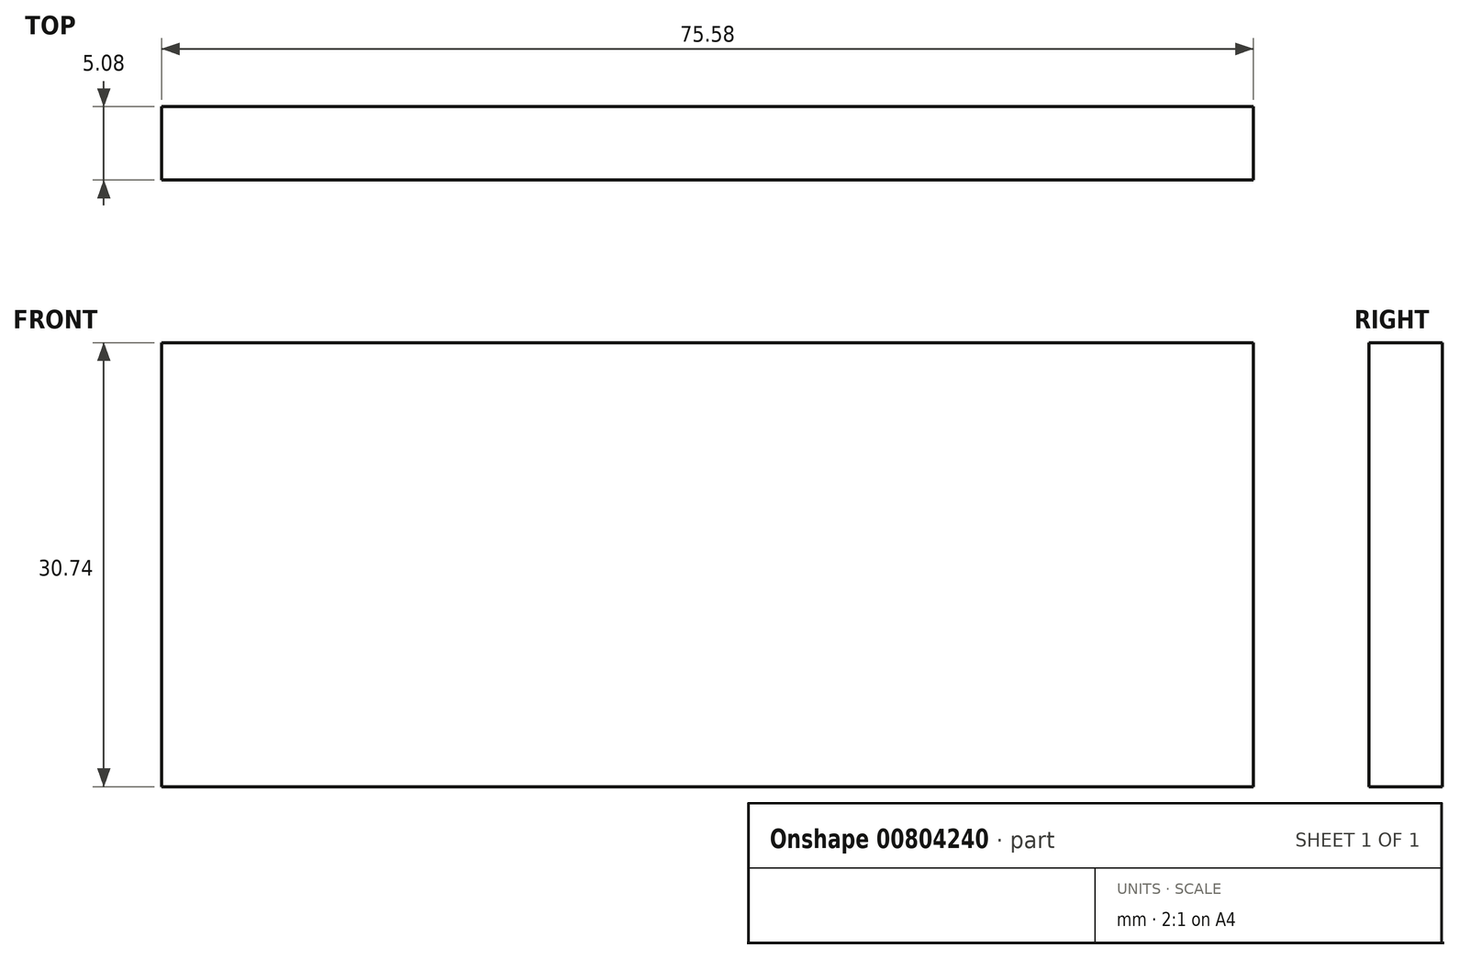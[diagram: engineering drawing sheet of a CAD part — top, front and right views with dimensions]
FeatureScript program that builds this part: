
annotation { "Feature Type Name" : "Feature", "Feature Type Description" : "" }
export const myFeature = defineFeature(function(context is Context, id is Id, definition is map)
    precondition{}
    {
        {
            var Q0;
            Q0=qCreatedBy(makeId("Front.planeOp"),FACE);
            var sketch = newSketch(context, id + "F0", { "sketchPlane" : qUnion([Q0])});
            skLineSegment(sketch, "E0.top", {"start": v(0, 30.74) * mm, "end": v(75.58, 30.74) * mm});
            skLineSegment(sketch, "E0.right", {"start": v(75.58, 0) * mm, "end": v(75.58, 30.74) * mm});
            skLineSegment(sketch, "E1", {"start": v(0, 30.74) * mm, "end": v(0, 0) * mm});
            skLineSegment(sketch, "E2", {"start": v(75.58, 0) * mm, "end": v(0, 0) * mm});
            skSolve(sketch);
        }
        {
            var Q0;
            Q0=makeQuery(id+"F0.imprint","IMPRINT",FACE,{"disambiguationData":[TD([[makeQuery(id+"F0.imprint","IMPRINT",EDGE,{"derivedFrom":sQuery(id+"F0.wireOp",EDGE,"E0.top")}),-1.0]])]});
            extrude(context, id + "F1", {"entities" : qUnion([Q0]), "depth" : 5.08 * mm, "offsetDistance" : 25.4 * mm});
        }
        {
            var Q0;
            Q0=qCreatedBy(makeId("Front.planeOp"),FACE);
            var sketch = newSketch(context, id + "F2", { "sketchPlane" : qUnion([Q0])});
            skLineSegment(sketch, "E3.bottom", {"start": v(6.42, 26.88) * mm, "end": v(69.57, 26.88) * mm});
            skLineSegment(sketch, "E3.top", {"start": v(6.42, 3.87) * mm, "end": v(69.57, 3.87) * mm});
            skLineSegment(sketch, "E3.left", {"start": v(6.42, 26.88) * mm, "end": v(6.42, 3.87) * mm});
            skLineSegment(sketch, "E3.right", {"start": v(69.57, 26.88) * mm, "end": v(69.57, 3.87) * mm});
            skSolve(sketch);
        }
        {
            var Q0;
            Q0 = qSketchRegion(id + "F2", true);
            extrude(context, id + "F3", {"entities" : qUnion([Q0]), "operationType" : NewBodyOperationType.ADD, "depth" : 3.17 * mm, "offsetDistance" : 25.4 * mm});
        }
    });
